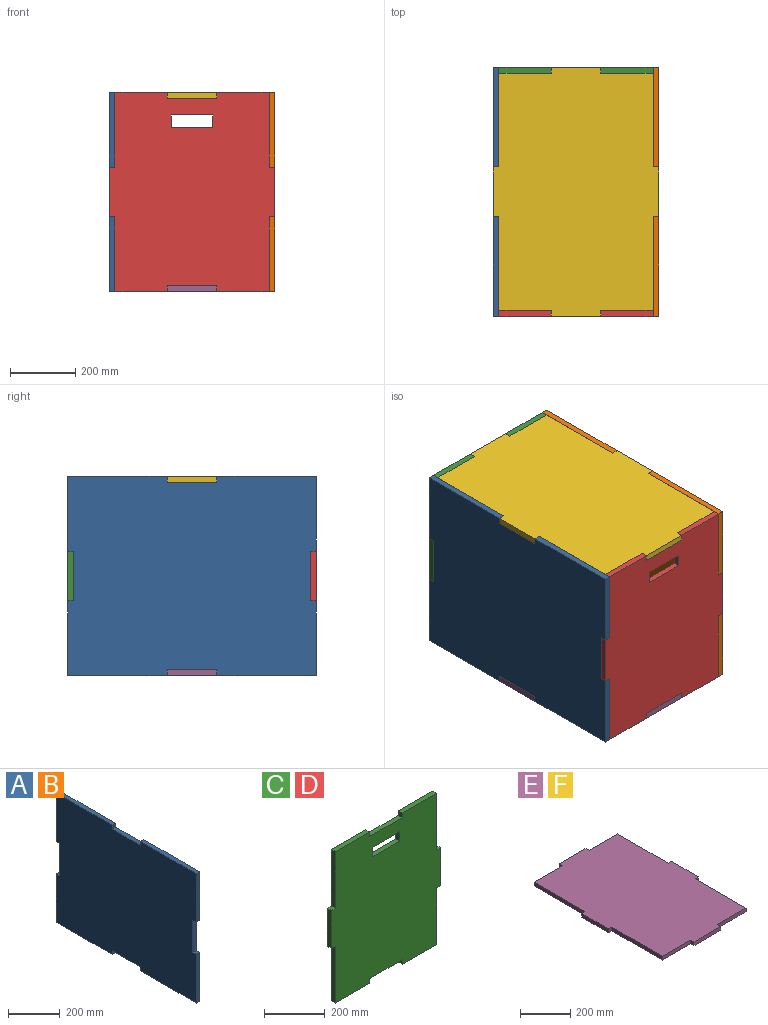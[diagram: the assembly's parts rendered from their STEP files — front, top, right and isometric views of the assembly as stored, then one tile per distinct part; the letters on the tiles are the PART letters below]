
ASSEMBLY  parts=6 mates=3
PART A: 22 faces, bbox 18.3x762x609.6 mm
  f0: plane 228.6x18.26mm, normal (0,1,0), area 4173.4mm2, adj f1,f19,f20,f21
  f1: plane 304.8x18.26mm, normal (0,0,1), area 5564.5mm2, adj f0,f2,f20,f21
  f2: plane 18.26x18.26mm, normal (0,-1,0), area 333.3mm2, adj f1,f3,f20,f21
  f3: plane 152.4x18.26mm, normal (0,0,1), area 2782.3mm2, adj f2,f4,f20,f21
  f4: plane 18.26x18.26mm, normal (0,1,0), area 333.3mm2, adj f3,f5,f20,f21
  f5: plane 304.8x18.26mm, normal (0,0,1), area 5564.5mm2, adj f4,f6,f20,f21
  f6: plane 228.6x18.26mm, normal (0,-1,0), area 4173.4mm2, adj f5,f7,f20,f21
  f7: plane 18.26x18.26mm, normal (0,0,-1), area 333.3mm2, adj f6,f8,f20,f21
  f8: plane 152.4x18.26mm, normal (0,-1,0), area 2782.3mm2, adj f7,f9,f20,f21
  f9: plane 18.26x18.26mm, normal (0,0,1), area 333.3mm2, adj f8,f10,f20,f21
  f10: plane 228.6x18.26mm, normal (0,-1,0), area 4173.4mm2, adj f9,f11,f20,f21
  f11: plane 304.8x18.26mm, normal (0,0,-1), area 5564.5mm2, adj f10,f12,f20,f21
  f12: plane 18.26x18.26mm, normal (0,1,0), area 333.3mm2, adj f11,f13,f20,f21
  f13: plane 152.4x18.26mm, normal (0,0,-1), area 2782.3mm2, adj f12,f14,f20,f21
  f14: plane 18.26x18.26mm, normal (0,-1,0), area 333.3mm2, adj f13,f15,f20,f21
  f15: plane 304.8x18.26mm, normal (0,0,-1), area 5564.5mm2, adj f14,f16,f20,f21
  f16: plane 228.6x18.26mm, normal (0,1,0), area 4173.4mm2, adj f15,f17,f20,f21
  f17: plane 18.26x18.26mm, normal (0,0,1), area 333.3mm2, adj f16,f18,f20,f21
  f18: plane 152.4x18.26mm, normal (0,1,0), area 2782.3mm2, adj f17,f19,f20,f21
  f19: plane 18.26x18.26mm, normal (0,0,-1), area 333.3mm2, adj f0,f18,f20,f21
  f20: plane 762x609.6mm, normal (1,0,0), area 453386.2mm2, adj f0,f1,f2,f3,f4,f5,f6,f7
  f21: plane 762x609.6mm, normal (-1,0,0), area 453386.2mm2, adj f0,f1,f2,f3,f4,f5,f6,f7
PART B: same geometry as A
PART C: 26 faces, bbox 508x18.3x609.6 mm
  f0: plane 152.4x18.26mm, normal (0,0,-1), area 2782.3mm2, adj f1,f23,f24,f25
  f1: plane 18.26x18.26mm, normal (-1,0,0), area 333.3mm2, adj f0,f2,f24,f25
  f2: plane 159.54x18.26mm, normal (0,0,-1), area 2912.7mm2, adj f1,f3,f24,f25
  f3: plane 228.6x18.26mm, normal (1,0,0), area 4173.4mm2, adj f2,f4,f24,f25
  f4: plane 18.26x18.26mm, normal (0,0,-1), area 333.3mm2, adj f3,f5,f24,f25
  f5: plane 152.4x18.26mm, normal (1,0,0), area 2782.3mm2, adj f4,f6,f24,f25
  f6: plane 18.26x18.26mm, normal (0,0,1), area 333.3mm2, adj f5,f7,f24,f25
  f7: plane 228.6x18.26mm, normal (1,0,0), area 4173.4mm2, adj f6,f8,f24,f25
  f8: plane 159.54x18.26mm, normal (0,0,1), area 2912.7mm2, adj f7,f9,f24,f25
  f9: plane 18.26x18.26mm, normal (-1,0,0), area 333.3mm2, adj f8,f10,f24,f25
  f10: plane 152.4x18.26mm, normal (0,0,1), area 2782.3mm2, adj f9,f11,f24,f25
  f11: plane 18.26x18.26mm, normal (1,0,0), area 333.3mm2, adj f10,f12,f24,f25
  f12: plane 159.54x18.26mm, normal (0,0,1), area 2912.7mm2, adj f11,f13,f24,f25
  f13: plane 228.6x18.26mm, normal (-1,0,0), area 4173.4mm2, adj f12,f14,f24,f25
  f14: plane 18.26x18.26mm, normal (0,0,1), area 333.3mm2, adj f13,f15,f24,f25
  f15: plane 152.4x18.26mm, normal (-1,0,0), area 2782.3mm2, adj f14,f16,f24,f25
  f16: plane 18.26x18.26mm, normal (0,0,-1), area 333.3mm2, adj f15,f17,f24,f25
  f17: plane 228.6x18.26mm, normal (-1,0,0), area 4173.4mm2, adj f16,f18,f24,f25
  f18: plane 159.54x18.26mm, normal (0,0,-1), area 2912.7mm2, adj f17,f23,f24,f25
  f19: plane 38.1x18.26mm, normal (1,0,0), area 695.6mm2, adj f20,f22,f24,f25
  f20: plane 127x18.26mm, normal (0,0,-1), area 2318.5mm2, adj f19,f21,f24,f25
  f21: plane 38.1x18.26mm, normal (-1,0,0), area 695.6mm2, adj f20,f22,f24,f25
  f22: plane 127x18.26mm, normal (0,0,1), area 2318.5mm2, adj f19,f21,f24,f25
  f23: plane 18.26x18.26mm, normal (1,0,0), area 333.3mm2, adj f0,f18,f24,f25
  f24: plane 609.6x508mm, normal (0,1,0), area 282580.1mm2, adj f0,f1,f2,f3,f4,f5,f6,f7
  f25: plane 609.6x508mm, normal (0,-1,0), area 282580.1mm2, adj f0,f1,f2,f3,f4,f5,f6,f7
PART D: same geometry as C
PART E: 22 faces, bbox 508x762x18.3 mm
  f0: plane 152.4x18.26mm, normal (0,-1,0), area 2782.3mm2, adj f1,f19,f20,f21
  f1: plane 18.26x18.26mm, normal (1,0,0), area 333.3mm2, adj f0,f2,f20,f21
  f2: plane 159.54x18.26mm, normal (0,-1,0), area 2912.7mm2, adj f1,f3,f20,f21
  f3: plane 286.54x18.26mm, normal (1,0,0), area 5231.2mm2, adj f2,f4,f20,f21
  f4: plane 18.26x18.26mm, normal (0,-1,0), area 333.3mm2, adj f3,f5,f20,f21
  f5: plane 152.4x18.26mm, normal (1,0,0), area 2782.3mm2, adj f4,f6,f20,f21
  f6: plane 18.26x18.26mm, normal (0,1,0), area 333.3mm2, adj f5,f7,f20,f21
  f7: plane 286.54x18.26mm, normal (1,0,0), area 5231.2mm2, adj f6,f8,f20,f21
  f8: plane 159.54x18.26mm, normal (0,1,0), area 2912.7mm2, adj f7,f9,f20,f21
  f9: plane 18.26x18.26mm, normal (1,0,0), area 333.3mm2, adj f8,f10,f20,f21
  f10: plane 152.4x18.26mm, normal (0,1,0), area 2782.3mm2, adj f9,f11,f20,f21
  f11: plane 18.26x18.26mm, normal (-1,0,0), area 333.3mm2, adj f10,f12,f20,f21
  f12: plane 159.54x18.26mm, normal (0,1,0), area 2912.7mm2, adj f11,f13,f20,f21
  f13: plane 286.54x18.26mm, normal (-1,0,0), area 5231.2mm2, adj f12,f14,f20,f21
  f14: plane 18.26x18.26mm, normal (0,1,0), area 333.3mm2, adj f13,f15,f20,f21
  f15: plane 152.4x18.26mm, normal (-1,0,0), area 2782.3mm2, adj f14,f16,f20,f21
  f16: plane 18.26x18.26mm, normal (0,-1,0), area 333.3mm2, adj f15,f17,f20,f21
  f17: plane 286.54x18.26mm, normal (-1,0,0), area 5231.2mm2, adj f16,f18,f20,f21
  f18: plane 159.54x18.26mm, normal (0,-1,0), area 2912.7mm2, adj f17,f19,f20,f21
  f19: plane 18.26x18.26mm, normal (-1,0,0), area 333.3mm2, adj f0,f18,f20,f21
  f20: plane 762x508mm, normal (0,0,1), area 353187.3mm2, adj f0,f1,f2,f3,f4,f5,f6,f7
  f21: plane 762x508mm, normal (0,0,-1), area 353187.3mm2, adj f0,f1,f2,f3,f4,f5,f6,f7
PART F: same geometry as E
PLACE A rot(axis=(0,0,-1),180deg) t=(-471.49,762,0)mm
PLACE B at identity
PLACE C rot(axis=(0,0,-1),180deg) t=(-471.49,762,0)mm
PLACE D at identity
PLACE E at identity
PLACE F rot(axis=(1,0,0),180deg) t=(0,762,609.6)mm
MATE fastened F.f6 <-> B.f4  axis (0,-1,0) through (9.13,304.8,600.47)mm
MATE fastened C.f14 <-> B.f19  axis (0,0,1) through (9.13,752.87,381)mm
MATE fastened A.f17 <-> D.f16  axis (0,0,1) through (-471.49,0,228.6)mm
